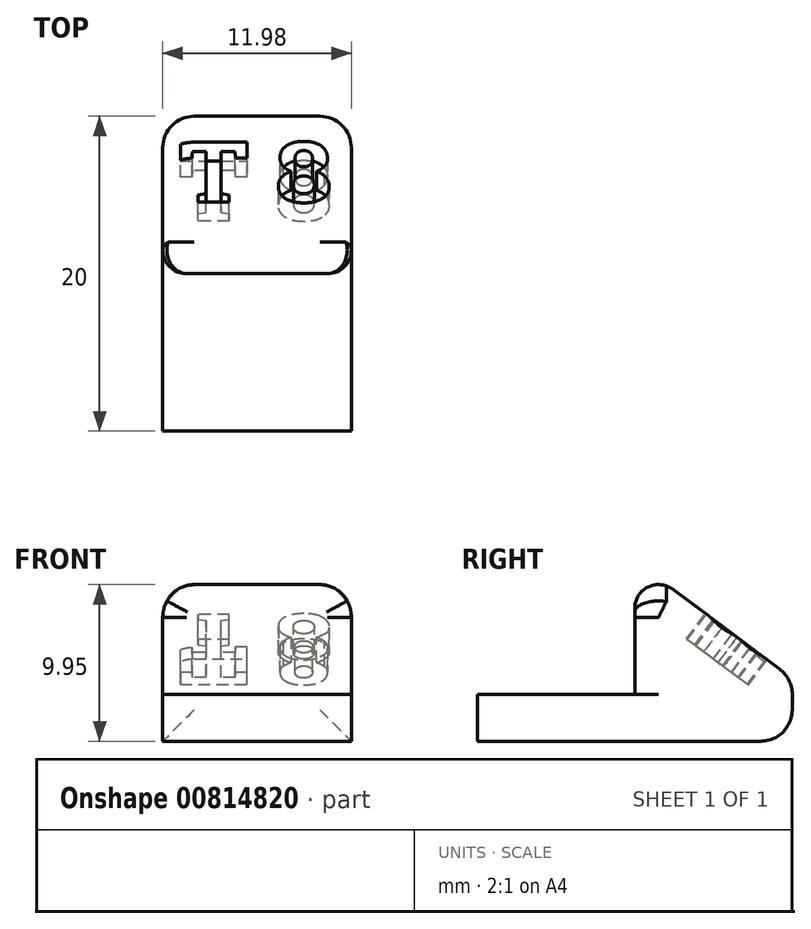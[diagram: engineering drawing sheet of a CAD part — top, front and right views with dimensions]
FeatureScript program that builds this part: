
annotation { "Feature Type Name" : "Feature", "Feature Type Description" : "" }
export const myFeature = defineFeature(function(context is Context, id is Id, definition is map)
    precondition{}
    {
        {
            var Q0;
            Q0=qCreatedBy(makeId("Top.planeOp"),FACE);
            var sketch = newSketch(context, id + "F0", { "sketchPlane" : qUnion([Q0])});
            skLineSegment(sketch, "E0.bottom", {"start": v(6, 10) * mm, "end": v(-5.99, 10) * mm});
            skLineSegment(sketch, "E0.top", {"start": v(6, -10) * mm, "end": v(-5.99, -10) * mm});
            skLineSegment(sketch, "E0.left", {"start": v(6, 10) * mm, "end": v(6, -10) * mm});
            skLineSegment(sketch, "E0.right", {"start": v(-5.99, 10) * mm, "end": v(-5.99, -10) * mm});
            skPoint(sketch, "E0.middle", {"position": v(0, 0) * mm});
            skSolve(sketch);
        }
        {
            var Q0;
            Q0=qSketchRegion(id+"F0",true);
            extrude(context, id + "F1", {"entities" : qUnion([Q0]), "depth" : 2.98 * mm, "offsetDistance" : 25 * mm});
        }
        {
            var Q0;
            Q0=makeQuery(id+"F1.opExtrude","CAP_FACE",FACE,{"disambiguationData":[OSD([sQuery(id+"F0.wireOp",EDGE,"E0.bottom"),sQuery(id+"F0.wireOp",EDGE,"E0.top"),sQuery(id+"F0.wireOp",EDGE,"E0.left"),sQuery(id+"F0.wireOp",EDGE,"E0.right")])],"isStart":false});
            var sketch = newSketch(context, id + "F2", { "sketchPlane" : qUnion([Q0])});
            skLineSegment(sketch, "E1.bottom", {"start": v(-5.99, 10) * mm, "end": v(6, 10) * mm});
            skLineSegment(sketch, "E1.top", {"start": v(-5.99, 0) * mm, "end": v(6, 0) * mm});
            skLineSegment(sketch, "E1.left", {"start": v(-5.99, 10) * mm, "end": v(-5.99, 0) * mm});
            skLineSegment(sketch, "E1.right", {"start": v(6, 10) * mm, "end": v(6, 0) * mm});
            skSolve(sketch);
        }
        {
            var Q0;
            Q0=makeQuery(id+"F2.imprint","IMPRINT",FACE,{"disambiguationData":[TD([[makeQuery(id+"F2.imprint","IMPRINT",EDGE,{"derivedFrom":sQuery(id+"F2.wireOp",EDGE,"E1.bottom")}),1.0]])]});
            extrude(context, id + "F3", {"entities" : qUnion([Q0]), "operationType" : NewBodyOperationType.ADD, "depth" : 7 * mm, "offsetDistance" : 25 * mm});
        }
        {
            var Q0;
            Q0=makeQuery(id+"F3.opExtrude","CAP_EDGE",EDGE,{"disambiguationData":[OSD([sQuery(id+"F2.wireOp",EDGE,"E1.bottom")])],"isStart":false});
            chamfer(context, id + "F4", {"entities" : qUnion([Q0]), "chamferType" : ChamferType.TWO_OFFSETS, "width1" : 8 * mm, "oppositeDirection" : false, "width2" : 6 * mm, "tangentPropagation" : true});
        }
        {
            var Q0;
            Q0=makeQuery(id+"F4.opChamfer","BLEND_FACE",FACE,{"disambiguationData":[OSD([sQuery(id+"F2.wireOp",EDGE,"E1.bottom")])]});
            var sketch = newSketch(context, id + "F5", { "sketchPlane" : qUnion([Q0])});
            skText(sketch, "E2", { "text": "T 8", "fontName": "RobotoSlab-Bold.ttf"});
            const initialGuessF5  = {"E2": [-0.005, -0.0012, 1, 0, 0.00481]};
            skSetInitialGuess(sketch, initialGuessF5);
            skSolve(sketch);
        }
        {
            var Q0;
            Q0 = qSketchRegion(id + "F5", true);
            extrude(context, id + "F6", {"entities" : qUnion([Q0]), "operationType" : NewBodyOperationType.REMOVE, "oppositeDirection" : true, "depth" : 2 * mm, "offsetDistance" : 25 * mm});
        }
        {
            var Q0;
            {var subQ0=sQuery(id+"F2.wireOp",EDGE,"E1.bottom");Q0=makeQuery(id+"F4.opChamfer","BLEND_EDGE",EDGE,{"blendedFrom":[makeQuery(id+"F3.opExtrude","CAP_EDGE",EDGE,{"disambiguationData":[OSD([subQ0])],"isStart":false}),makeQuery(id+"F3.boolean.opBoolean","MERGE",FACE,{"derivedFrom":[makeQuery(id+"F1.opExtrude","SWEPT_FACE",FACE,{"disambiguationData":[OSD([sQuery(id+"F0.wireOp",EDGE,"E0.bottom")])]}),makeQuery(id+"F3.opExtrude","SWEPT_FACE",FACE,{"disambiguationData":[OSD([subQ0])]})]})],"blendedInto":[makeQuery(id+"F3.boolean.opBoolean","MERGE",FACE,{"derivedFrom":[makeQuery(id+"F1.opExtrude","SWEPT_FACE",FACE,{"disambiguationData":[OSD([sQuery(id+"F0.wireOp",EDGE,"E0.bottom")])]}),makeQuery(id+"F3.opExtrude","SWEPT_FACE",FACE,{"disambiguationData":[OSD([subQ0])]})]})]});}
            var Q1;
            Q1=makeQuery(id+"F1.opExtrude","CAP_EDGE",EDGE,{"disambiguationData":[OSD([sQuery(id+"F0.wireOp",EDGE,"E0.bottom")])],"isStart":true});
            var Q2;
            Q2=makeQuery(id+"F3.boolean.opBoolean","MERGE",EDGE,{"derivedFrom":[makeQuery(id+"F1.opExtrude","SWEPT_EDGE",EDGE,{"disambiguationData":[OSD([sQuery(id+"F0.wireOp",EDGE,"E0.bottom"),sQuery(id+"F0.wireOp",EDGE,"E0.left")])]}),makeQuery(id+"F3.opExtrude","SWEPT_EDGE",EDGE,{"disambiguationData":[OSD([sQuery(id+"F2.wireOp",EDGE,"E1.bottom"),sQuery(id+"F2.wireOp",EDGE,"E1.right")])]})]});
            var Q3;
            Q3=makeQuery(id+"F3.boolean.opBoolean","MERGE",EDGE,{"derivedFrom":[makeQuery(id+"F1.opExtrude","SWEPT_EDGE",EDGE,{"disambiguationData":[OSD([sQuery(id+"F0.wireOp",EDGE,"E0.bottom"),sQuery(id+"F0.wireOp",EDGE,"E0.right")])]}),makeQuery(id+"F3.opExtrude","SWEPT_EDGE",EDGE,{"disambiguationData":[OSD([sQuery(id+"F2.wireOp",EDGE,"E1.bottom"),sQuery(id+"F2.wireOp",EDGE,"E1.left")])]})]});
            var Q4;
            Q4=makeQuery(id+"F4.opChamfer","BLEND_EDGE",EDGE,{"blendedFrom":[makeQuery(id+"F3.opExtrude","CAP_EDGE",EDGE,{"disambiguationData":[OSD([sQuery(id+"F2.wireOp",EDGE,"E1.bottom")])],"isStart":false}),makeQuery(id+"F3.boolean.opBoolean","MERGE",FACE,{"derivedFrom":[makeQuery(id+"F1.opExtrude","SWEPT_FACE",FACE,{"disambiguationData":[OSD([sQuery(id+"F0.wireOp",EDGE,"E0.right")])]}),makeQuery(id+"F3.opExtrude","SWEPT_FACE",FACE,{"disambiguationData":[OSD([sQuery(id+"F2.wireOp",EDGE,"E1.left")])]})]})],"blendedInto":[makeQuery(id+"F3.boolean.opBoolean","MERGE",FACE,{"derivedFrom":[makeQuery(id+"F1.opExtrude","SWEPT_FACE",FACE,{"disambiguationData":[OSD([sQuery(id+"F0.wireOp",EDGE,"E0.right")])]}),makeQuery(id+"F3.opExtrude","SWEPT_FACE",FACE,{"disambiguationData":[OSD([sQuery(id+"F2.wireOp",EDGE,"E1.left")])]})]})]});
            var Q5;
            Q5=makeQuery(id+"F4.opChamfer","BLEND_EDGE",EDGE,{"blendedFrom":[makeQuery(id+"F3.opExtrude","CAP_EDGE",EDGE,{"disambiguationData":[OSD([sQuery(id+"F2.wireOp",EDGE,"E1.bottom")])],"isStart":false}),makeQuery(id+"F3.boolean.opBoolean","MERGE",FACE,{"derivedFrom":[makeQuery(id+"F1.opExtrude","SWEPT_FACE",FACE,{"disambiguationData":[OSD([sQuery(id+"F0.wireOp",EDGE,"E0.left")])]}),makeQuery(id+"F3.opExtrude","SWEPT_FACE",FACE,{"disambiguationData":[OSD([sQuery(id+"F2.wireOp",EDGE,"E1.right")])]})]})],"blendedInto":[makeQuery(id+"F3.boolean.opBoolean","MERGE",FACE,{"derivedFrom":[makeQuery(id+"F1.opExtrude","SWEPT_FACE",FACE,{"disambiguationData":[OSD([sQuery(id+"F0.wireOp",EDGE,"E0.left")])]}),makeQuery(id+"F3.opExtrude","SWEPT_FACE",FACE,{"disambiguationData":[OSD([sQuery(id+"F2.wireOp",EDGE,"E1.right")])]})]})]});
            var Q6;
            Q6=makeQuery(id+"F3.opExtrude","CAP_EDGE",EDGE,{"disambiguationData":[OSD([sQuery(id+"F2.wireOp",EDGE,"E1.right")])],"isStart":false});
            var Q7;
            Q7=makeQuery(id+"F3.opExtrude","CAP_EDGE",EDGE,{"disambiguationData":[OSD([sQuery(id+"F2.wireOp",EDGE,"E1.left")])],"isStart":false});
            var Q8;
            {var subQ0=sQuery(id+"F2.wireOp",EDGE,"E1.bottom");Q8=makeQuery(id+"F4.opChamfer","BLEND_EDGE",EDGE,{"blendedFrom":[makeQuery(id+"F3.opExtrude","CAP_EDGE",EDGE,{"disambiguationData":[OSD([subQ0])],"isStart":false}),makeQuery(id+"F3.opExtrude","CAP_FACE",FACE,{"disambiguationData":[OSD([subQ0,sQuery(id+"F2.wireOp",EDGE,"E1.top"),sQuery(id+"F2.wireOp",EDGE,"E1.left"),sQuery(id+"F2.wireOp",EDGE,"E1.right")])],"isStart":false})],"blendedInto":[makeQuery(id+"F3.opExtrude","CAP_FACE",FACE,{"disambiguationData":[OSD([subQ0,sQuery(id+"F2.wireOp",EDGE,"E1.top"),sQuery(id+"F2.wireOp",EDGE,"E1.left"),sQuery(id+"F2.wireOp",EDGE,"E1.right")])],"isStart":false})]});}
            fillet(context, id + "F7", {"entities" : qUnion([Q0, Q1, Q2, Q3, Q4, Q5, Q6, Q7, Q8]), "radius" : 2 * mm, "tangentPropagation" : true, "allowEdgeOverflow" : false});
        }
        {
            var Q0;
            Q0=makeQuery(id+"F3.opExtrude","CAP_EDGE",EDGE,{"disambiguationData":[OSD([sQuery(id+"F2.wireOp",EDGE,"E1.top")])],"isStart":false});
            fillet(context, id + "F8", {"entities" : qUnion([Q0]), "radius" : 1.5 * mm, "tangentPropagation" : true, "allowEdgeOverflow" : false});
        }
    });
